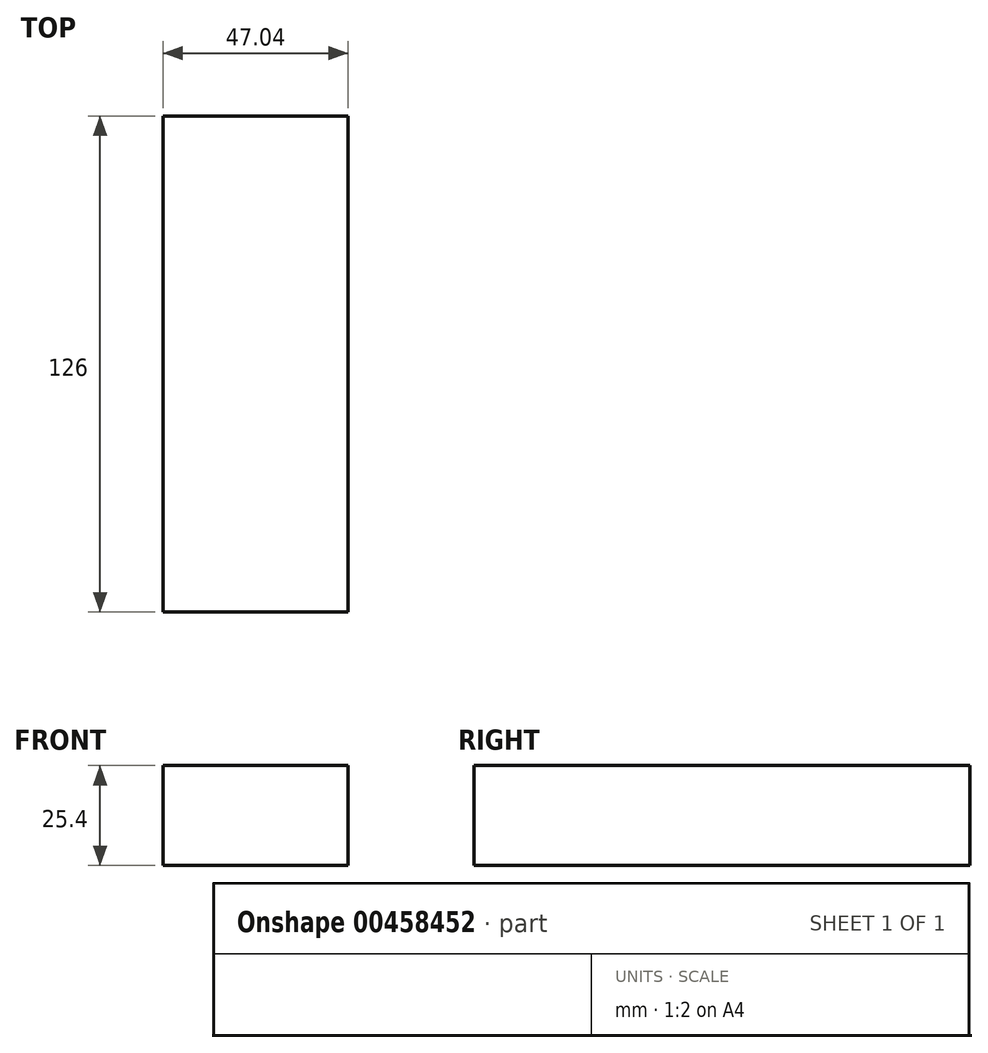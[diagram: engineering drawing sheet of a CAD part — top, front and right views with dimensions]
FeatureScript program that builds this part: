
annotation { "Feature Type Name" : "Feature", "Feature Type Description" : "" }
export const myFeature = defineFeature(function(context is Context, id is Id, definition is map)
    precondition{}
    {
        {
            var Q0;
            Q0=qCreatedBy(makeId("Top.planeOp"),FACE);
            var sketch = newSketch(context, id + "F0", { "sketchPlane" : qUnion([Q0])});
            skLineSegment(sketch, "E0.bottom", {"start": v(47.04, -46.24) * mm, "end": v(0, -46.24) * mm});
            skLineSegment(sketch, "E0.top", {"start": v(47.04, 79.76) * mm, "end": v(0, 79.76) * mm});
            skLineSegment(sketch, "E0.left", {"start": v(47.04, -46.24) * mm, "end": v(47.04, 79.76) * mm});
            skLineSegment(sketch, "E0.right", {"start": v(0, -46.24) * mm, "end": v(0, 79.76) * mm});
            skLineSegment(sketch, "E1.bottom", {"start": v(91.91, -36.26) * mm, "end": v(47.04, -36.26) * mm});
            skLineSegment(sketch, "E1.top", {"start": v(91.91, -46.24) * mm, "end": v(47.04, -46.24) * mm});
            skLineSegment(sketch, "E1.left", {"start": v(91.91, -36.26) * mm, "end": v(91.91, -46.24) * mm});
            skLineSegment(sketch, "E1.right", {"start": v(47.04, -36.26) * mm, "end": v(47.04, -46.24) * mm});
            skSolve(sketch);
        }
        {
            var Q0;
            Q0 = qSketchRegion(id + "F0", true);
            var sketch = newSketch(context, id + "F1", { "sketchPlane" : qUnion([Q0])});
            skSolve(sketch);
        }
        {
            var Q0;
            Q0=makeQuery(id+"F1.imprint","IMPRINT",FACE,{"disambiguationData":[TD([[makeQuery(id+"F1.imprint","IMPRINT",EDGE,{"derivedFrom":makeQuery(id+"F0.imprint","IMPRINT",EDGE,{"derivedFrom":sQuery(id+"F0.wireOp",EDGE,"E0.bottom")})}),-1.0]])]});
            var sketch = newSketch(context, id + "F2", { "sketchPlane" : qUnion([Q0])});
            skSolve(sketch);
        }
        {
            var Q0;
            Q0=makeQuery(id+"F2.imprint","IMPRINT",FACE,{"disambiguationData":[TD([[makeQuery(id+"F2.imprint","IMPRINT",EDGE,{"derivedFrom":makeQuery(id+"F1.imprint","IMPRINT",EDGE,{"derivedFrom":makeQuery(id+"F0.imprint","IMPRINT",EDGE,{"derivedFrom":sQuery(id+"F0.wireOp",EDGE,"E0.bottom")})})}),-1.0]])]});
            extrude(context, id + "F3", {"entities" : qUnion([Q0]), "depth" : 25.4 * mm});
        }
    });
